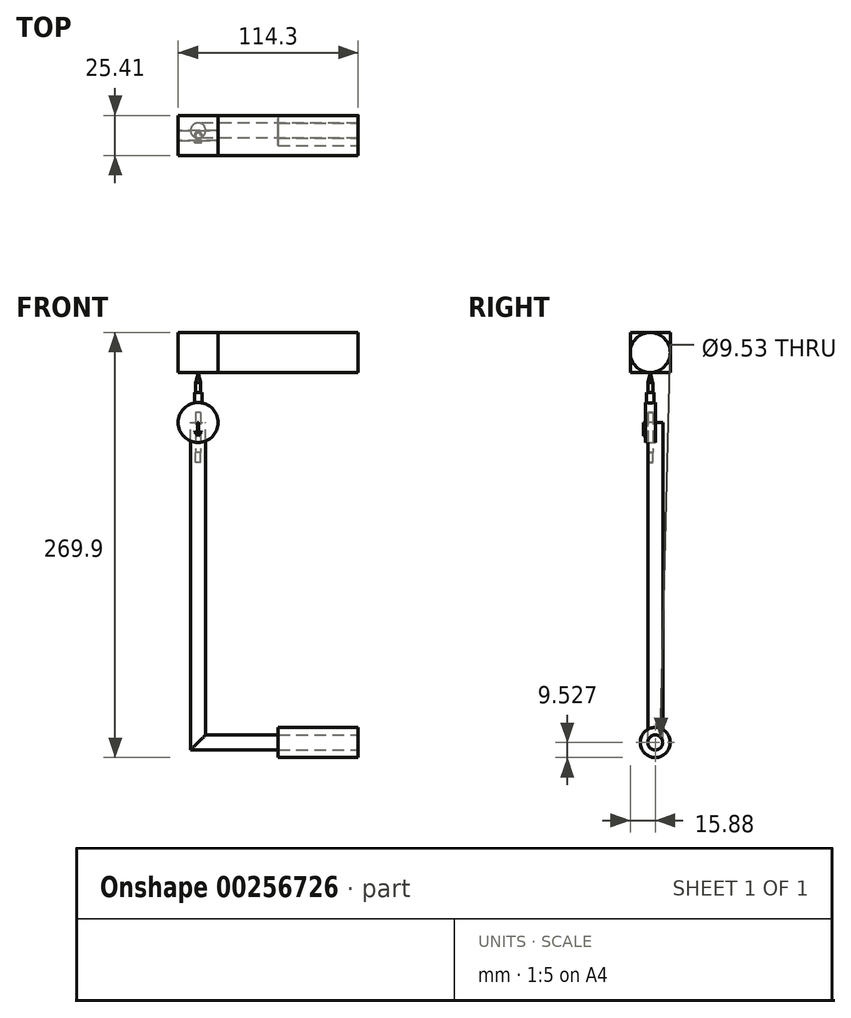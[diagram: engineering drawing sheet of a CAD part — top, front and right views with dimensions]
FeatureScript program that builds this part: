
annotation { "Feature Type Name" : "Feature", "Feature Type Description" : "" }
export const myFeature = defineFeature(function(context is Context, id is Id, definition is map)
    precondition{}
    {
        {
            var Q0;
            Q0=qCreatedBy(makeId("Front.planeOp"),FACE);
            var sketch = newSketch(context, id + "F0", { "sketchPlane" : qUnion([Q0])});
            skCircle(sketch, "E0", {"center": v(0, 0) * mm, "radius": 12.7 * mm});
            skSolve(sketch);
        }
        {
            var Q0;
            Q0=makeQuery(id+"F0.imprint","IMPRINT",FACE,{"disambiguationData":[TD([[makeQuery(id+"F0.imprint","IMPRINT",EDGE,{"derivedFrom":sQuery(id+"F0.wireOp",EDGE,"E0")}),1.0]])]});
            extrude(context, id + "F1", {"entities" : qUnion([Q0]), "depth" : 6.35 * mm, "offsetDistance" : 25.4 * mm});
        }
        {
            var Q0;
            Q0=qCreatedBy(makeId("Top.planeOp"),FACE);
            var sketch = newSketch(context, id + "F2", { "sketchPlane" : qUnion([Q0])});
            skLineSegment(sketch, "E1", {"start": v(0, 0) * mm, "end": v(0, -6.35) * mm, "construction": true});
            skCircle(sketch, "E2", {"center": v(0, -3.18) * mm, "radius": 2.38 * mm});
            skSolve(sketch);
        }
        {
            var Q0;
            Q0 = qSketchRegion(id + "F2", true);
            extrude(context, id + "F3", {"entities" : qUnion([Q0]), "operationType" : NewBodyOperationType.ADD, "depth" : 19.05 * mm, "offsetDistance" : 25.4 * mm});
        }
        {
            var Q0;
            Q0=makeQuery(id+"F3.opExtrude","CAP_FACE",FACE,{"disambiguationData":[OSD([sQuery(id+"F2.wireOp",EDGE,"E2")])],"isStart":false});
            var sketch = newSketch(context, id + "F4", { "sketchPlane" : qUnion([Q0])});
            skCircle(sketch, "E3", {"center": v(0, -3.17) * mm, "radius": 1.59 * mm});
            skSolve(sketch);
        }
        {
            var Q0;
            Q0=makeQuery(id+"F4.imprint","IMPRINT",FACE,{"disambiguationData":[TD([[makeQuery(id+"F4.imprint","IMPRINT",EDGE,{"derivedFrom":sQuery(id+"F4.wireOp",EDGE,"E3")}),1.0]])]});
            extrude(context, id + "F5", {"entities" : qUnion([Q0]), "depth" : 6.35 * mm, "offsetDistance" : 25.4 * mm});
        }
        {
            var Q0;
            Q0=makeQuery(id+"F5.opExtrude","CAP_FACE",FACE,{"disambiguationData":[OSD([sQuery(id+"F4.wireOp",EDGE,"E3")])],"isStart":false});
            cPlane(context, id + "F6", {"entities" : qUnion([Q0]), "cplaneType" : CPlaneType.OFFSET, "offset" : 6.35 * mm, "width" : 152.4 * mm, "height" : 152.4 * mm});
        }
        {
            var Q0;
            Q0=qCreatedBy(id+"F6.planeOp",FACE);
            var sketch = newSketch(context, id + "F7", { "sketchPlane" : qUnion([Q0])});
            skLineSegment(sketch, "E4", {"start": v(0, -3.15) * mm, "end": v(1.02, -3.15) * mm, "construction": true});
            skLineSegment(sketch, "E5", {"start": v(1.02, -3.15) * mm, "end": v(0, -3.15) * mm, "construction": true});
            skCircle(sketch, "E6", {"center": v(0, -3.15) * mm, "radius": 0.01 * mm});
            skSolve(sketch);
        }
        {
            var Q0;
            Q0=makeQuery(id+"F5.opExtrude","CAP_FACE",FACE,{"disambiguationData":[OSD([sQuery(id+"F4.wireOp",EDGE,"E3")])],"isStart":false});
            var Q1;
            Q1=sQuery(id+"F7.wireOp",VERTEX,"E4.start");
            loft(context, id + "F8", {"sheetProfilesArray" : [{ "sheetProfileEntities" : qUnion([Q0]) }, { "sheetProfileEntities" : qUnion([Q1]) }]});
        }
        {
            var Q0;
            Q0=makeQuery(id+"F5.opExtrude","SWEPT_BODY",BODY,{"disambiguationData":[OSD([sQuery(id+"F4.wireOp",EDGE,"E3")])]});
            var Q1;
            Q1=qCreatedBy(makeId("Top.planeOp"),FACE);
            mirror(context, id + "F9", {"entities" : qUnion([Q0]), "mirrorPlane" : qUnion([Q1])});
        }
        {
            var Q0;
            Q0=makeQuery(id+"F9.opPattern","COPY",FACE,{"derivedFrom":makeQuery(id+"F5.opExtrude","CAP_FACE",FACE,{"disambiguationData":[OSD([sQuery(id+"F4.wireOp",EDGE,"E3")])],"isStart":true}),"instanceName":"1"});
            extrude(context, id + "F10", {"entities" : qUnion([Q0]), "depth" : 25.4 * mm, "offsetDistance" : 25.4 * mm});
        }
        {
            var Q0;
            Q0=makeQuery(id+"F1.opExtrude","CAP_FACE",FACE,{"disambiguationData":[OSD([sQuery(id+"F0.wireOp",EDGE,"E0")])],"isStart":false});
            var sketch = newSketch(context, id + "F11", { "sketchPlane" : qUnion([Q0])});
            skLineSegment(sketch, "E7", {"start": v(0, -8.7) * mm, "end": v(2.25, -5.86) * mm});
            skLineSegment(sketch, "E8", {"start": v(2.25, -5.86) * mm, "end": v(1.84, -5.53) * mm});
            skLineSegment(sketch, "E9", {"start": v(1.84, -5.53) * mm, "end": v(0.37, -7.38) * mm});
            skLineSegment(sketch, "E10", {"start": v(0.37, -7.38) * mm, "end": v(0.37, 0) * mm});
            skLineSegment(sketch, "E11.MirrorCS", {"start": v(0, -8.7) * mm, "end": v(-2.25, -5.86) * mm});
            skLineSegment(sketch, "E12.MirrorCS", {"start": v(-1.84, -5.53) * mm, "end": v(-0.37, -7.38) * mm});
            skLineSegment(sketch, "E13.MirrorCS", {"start": v(-0.37, -7.38) * mm, "end": v(-0.37, 0) * mm});
            skLineSegment(sketch, "E14.MirrorCS", {"start": v(-2.25, -5.86) * mm, "end": v(-1.84, -5.53) * mm});
            skLineSegment(sketch, "E15", {"start": v(0.37, 0) * mm, "end": v(-0.37, 0) * mm});
            skSolve(sketch);
        }
        {
            var Q0;
            Q0=makeQuery(id+"F11.imprint","IMPRINT",FACE,{"disambiguationData":[TD([[makeQuery(id+"F11.imprint","IMPRINT",EDGE,{"derivedFrom":sQuery(id+"F11.wireOp",EDGE,"E7")}),1.0]])]});
            extrude(context, id + "F12", {"entities" : qUnion([Q0]), "depth" : 1.27 * mm, "offsetDistance" : 25.4 * mm});
        }
        {
            var Q0;
            Q0=qCreatedBy(makeId("Front.planeOp"),FACE);
            var sketch = newSketch(context, id + "F13", { "sketchPlane" : qUnion([Q0])});
            skLineSegment(sketch, "E16", {"start": v(0, 0) * mm, "end": v(0, -203.2) * mm});
            skLineSegment(sketch, "E17", {"start": v(0, -203.2) * mm, "end": v(101.6, -203.2) * mm});
            skSolve(sketch);
        }
        {
            var Q0;
            Q0=sQuery(id+"F13.wireOp",VERTEX,"E17.end");
            var Q1;
            Q1=sQuery(id+"F13.wireOp",EDGE,"E17");
            cPlane(context, id + "F14", {"entities" : qUnion([Q0, Q1]), "cplaneType" : CPlaneType.LINE_POINT, "offset" : 25.4 * mm, "width" : 152.4 * mm, "height" : 152.4 * mm});
        }
        {
            var Q0;
            Q0=qCreatedBy(id+"F14.planeOp",FACE);
            var sketch = newSketch(context, id + "F15", { "sketchPlane" : qUnion([Q0])});
            skCircle(sketch, "E18", {"center": v(0, -203.22) * mm, "radius": 4.76 * mm});
            skSolve(sketch);
        }
        {
            var Q0;
            Q0=makeQuery(id+"F15.imprint","IMPRINT",FACE,{"disambiguationData":[TD([[makeQuery(id+"F15.imprint","IMPRINT",EDGE,{"derivedFrom":sQuery(id+"F15.wireOp",EDGE,"E18")}),1.0]])]});
            var Q1;
            Q1=sQuery(id+"F13.wireOp",EDGE,"E17");
            var Q2;
            Q2=sQuery(id+"F13.wireOp",EDGE,"E16");
            sweep(context, id + "F16", {"profiles" : qUnion([Q0]), "path" : qUnion([Q1, Q2])});
        }
        {
            var Q0;
            Q0=makeQuery(id+"F16.opSweep","CAP_FACE",FACE,{"disambiguationData":[OSD([sQuery(id+"F13.wireOp",VERTEX,"E17.end"),sQuery(id+"F15.wireOp",EDGE,"E18")])],"isStart":true});
            var sketch = newSketch(context, id + "F17", { "sketchPlane" : qUnion([Q0])});
            skCircle(sketch, "E19", {"center": v(0, -203.22) * mm, "radius": 9.53 * mm});
            skSolve(sketch);
        }
        {
            var Q0;
            Q0=makeQuery(id+"F17.imprint","IMPRINT",FACE,{"disambiguationData":[TD([[makeQuery(id+"F17.imprint","IMPRINT",EDGE,{"derivedFrom":sQuery(id+"F17.wireOp",EDGE,"E19")}),1.0]])]});
            extrude(context, id + "F18", {"entities" : qUnion([Q0]), "oppositeDirection" : true, "depth" : 50.8 * mm, "offsetDistance" : 25.4 * mm});
        }
        {
            var Q0;
            Q0=qCreatedBy(id+"F6.planeOp",FACE);
            var sketch = newSketch(context, id + "F19", { "sketchPlane" : qUnion([Q0])});
            skLineSegment(sketch, "E20.bottom", {"start": v(12.7, 9.52) * mm, "end": v(-12.7, 9.52) * mm});
            skLineSegment(sketch, "E20.top", {"start": v(12.7, -15.88) * mm, "end": v(-12.7, -15.88) * mm});
            skLineSegment(sketch, "E20.left", {"start": v(12.7, 9.52) * mm, "end": v(12.7, -15.88) * mm});
            skLineSegment(sketch, "E20.right", {"start": v(-12.7, 9.52) * mm, "end": v(-12.7, -15.88) * mm});
            skPoint(sketch, "E20.middle", {"position": v(0, -3.18) * mm});
            skSolve(sketch);
        }
        {
            var Q0;
            Q0=makeQuery(id+"F19.imprint","IMPRINT",FACE,{"disambiguationData":[TD([[makeQuery(id+"F19.imprint","IMPRINT",EDGE,{"derivedFrom":sQuery(id+"F19.wireOp",EDGE,"E20.bottom")}),1.0]])]});
            extrude(context, id + "F20", {"entities" : qUnion([Q0]), "depth" : 25.4 * mm, "offsetDistance" : 25.4 * mm});
        }
        {
            var Q0;
            Q0=makeQuery(id+"F20.opExtrude","SWEPT_FACE",FACE,{"disambiguationData":[OSD([sQuery(id+"F19.wireOp",EDGE,"E20.left")])]});
            var sketch = newSketch(context, id + "F21", { "sketchPlane" : qUnion([Q0])});
            skLineSegment(sketch, "E21", {"start": v(-15.88, 31.75) * mm, "end": v(9.52, 57.15) * mm, "construction": true});
            skCircle(sketch, "E22", {"center": v(-3.18, 44.45) * mm, "radius": 12.7 * mm});
            skSolve(sketch);
        }
        {
            var Q0;
            {var subQ0=sQuery(id+"F21.wireOp",EDGE,"E22");var subQ1=sQuery(id+"F19.wireOp",EDGE,"E20.left");var subQ2=makeQuery(id+"F21.imprint","INTERSECT",VERTEX,{"derivedFrom":[makeQuery(id+"F20.opExtrude","CAP_EDGE",EDGE,{"disambiguationData":[OSD([subQ1])],"isStart":false}),subQ0]});Q0=makeQuery(id+"F21.imprint","IMPRINT",FACE,{"disambiguationData":[TD([[makeQuery(id+"F21.imprint","IMPRINT",EDGE,{"disambiguationData":[TD([[subQ2,1.0]])],"derivedFrom":subQ0}),1.0]])]});}
            extrude(context, id + "F22", {"entities" : qUnion([Q0]), "operationType" : NewBodyOperationType.ADD, "depth" : 88.9 * mm, "offsetDistance" : 25.4 * mm});
        }
    });
